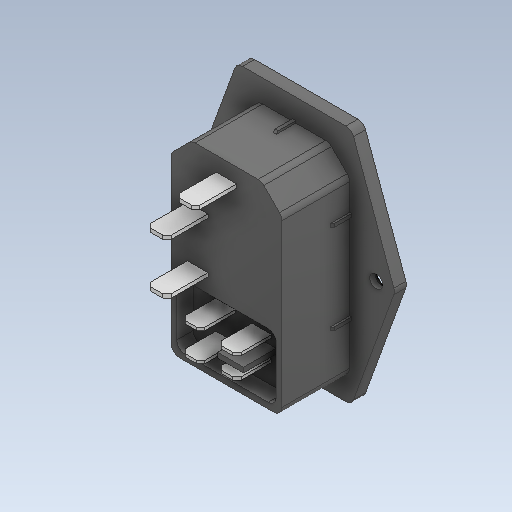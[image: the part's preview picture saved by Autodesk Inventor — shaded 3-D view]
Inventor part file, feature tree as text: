
AUTODESK INVENTOR PART (.ipt)
format: ipt  version: 2020 (Build 240168000, 168)  size: 261,632 bytes
history: native  units: in
note: dims shown in document units (in); Inventor stores cm internally (conversion verified against a paired STEP export)
features: chamfer x1
ambient origin geometry x8: Origin, YZ Plane, XZ Plane, XY Plane, X Axis, Y Axis, Z Axis, Center Point
bodies: Solid1 (feature_tree)
feature tree (1):
  chamfer  "Chamfer4"  [1 undecoded]
note: 1 required parameter value undecoded (feature->parameter linkage not recoverable at this tier; creation-order binding heuristic only, values carry confidence <= 0.55)
